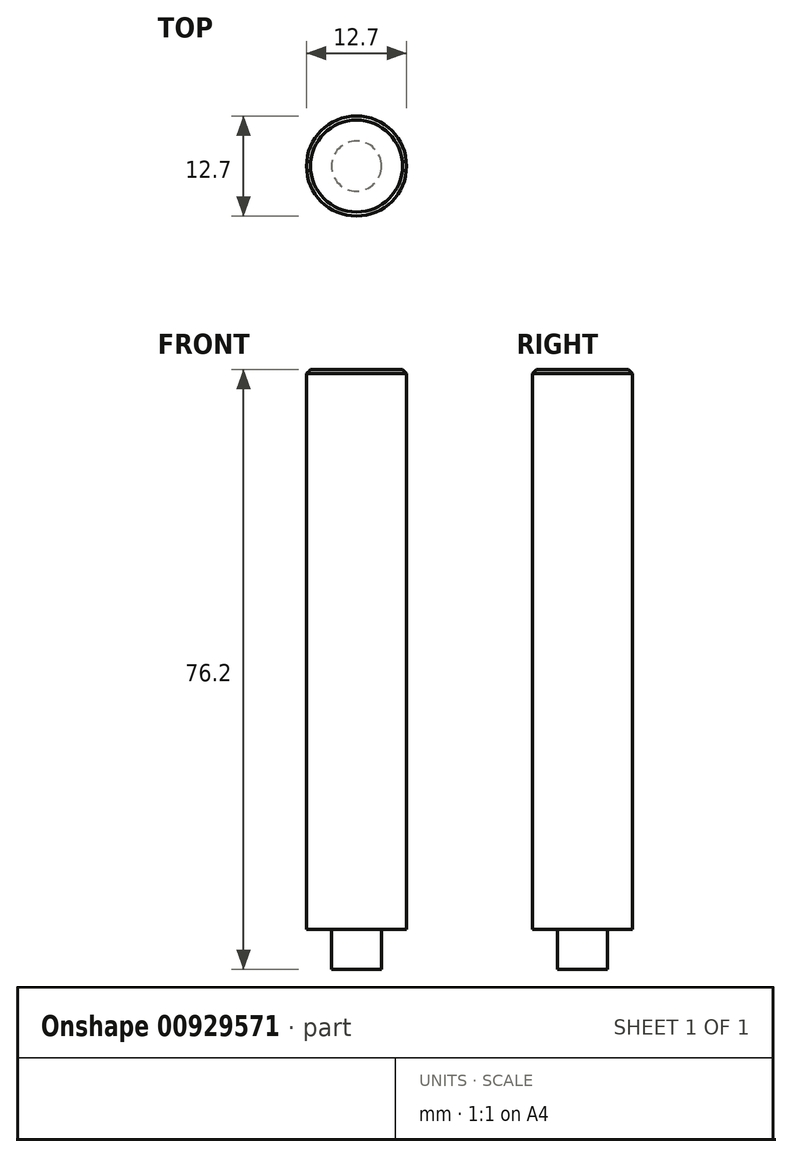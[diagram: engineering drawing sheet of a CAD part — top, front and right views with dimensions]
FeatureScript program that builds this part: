
annotation { "Feature Type Name" : "Feature", "Feature Type Description" : "" }
export const myFeature = defineFeature(function(context is Context, id is Id, definition is map)
    precondition{}
    {
        {
            var Q0;
            Q0=qCreatedBy(makeId("Front.planeOp"),FACE);
            var sketch = newSketch(context, id + "F0", { "sketchPlane" : qUnion([Q0])});
            skLineSegment(sketch, "E0", {"start": v(0, 0) * mm, "end": v(0, 76.2) * mm});
            skLineSegment(sketch, "E1", {"start": v(0, 76.2) * mm, "end": v(6.35, 76.2) * mm});
            skLineSegment(sketch, "E2", {"start": v(6.35, 76.2) * mm, "end": v(6.35, 5.08) * mm});
            skLineSegment(sketch, "E3", {"start": v(6.35, 5.08) * mm, "end": v(3.17, 5.08) * mm});
            skLineSegment(sketch, "E4", {"start": v(3.17, 5.08) * mm, "end": v(3.18, 0) * mm});
            skLineSegment(sketch, "E5", {"start": v(3.17, 0) * mm, "end": v(0, 0) * mm});
            skSolve(sketch);
        }
        {
            var Q0;
            Q0 = qSketchRegion(id + "F0", true);
            var Q1;
            Q1=sQuery(id+"F0.wireOp",EDGE,"E0");
            revolve(context, id + "F1", {"surfaceOperationType" : NewSurfaceOperationType.NEW, "entities" : qUnion([Q0]), "axis" : qUnion([Q1]), "revolveType" : RevolveType.FULL});
        }
        {
            var Q0;
            Q0=makeQuery(id+"F1.opRevolve","SWEPT_EDGE",EDGE,{"disambiguationData":[OSD([sQuery(id+"F0.wireOp",EDGE,"E1"),sQuery(id+"F0.wireOp",EDGE,"E2")])]});
            chamfer(context, id + "F2", {"entities" : qUnion([Q0]), "width" : 0.5 * mm, "tangentPropagation" : true});
        }
    });
